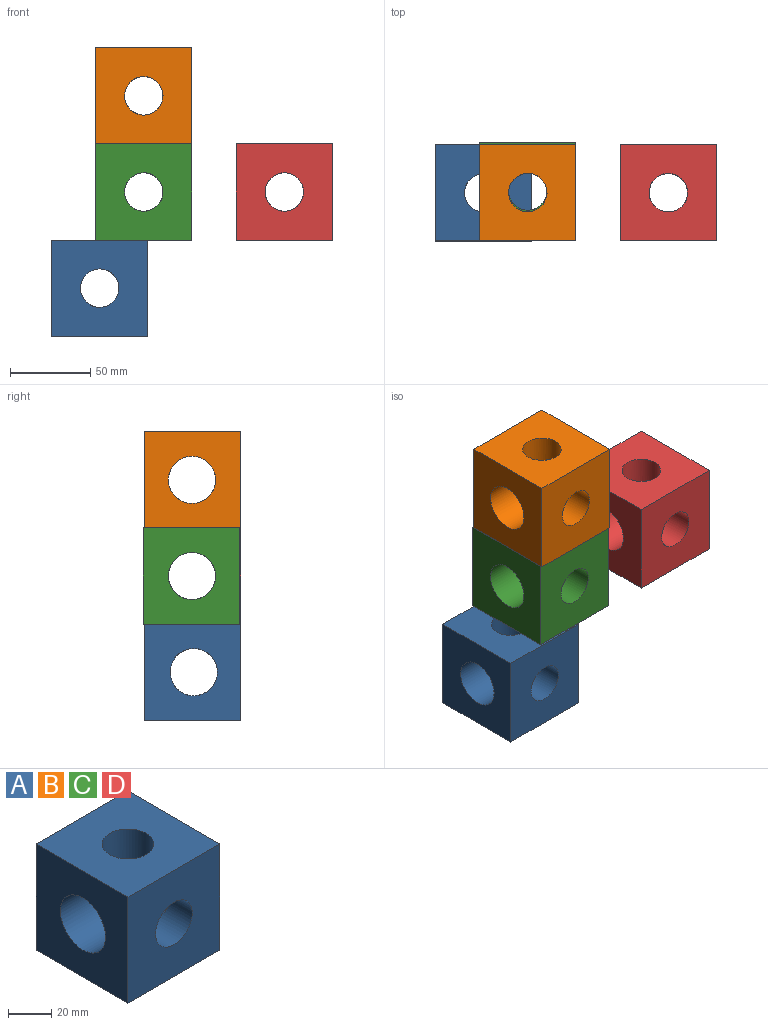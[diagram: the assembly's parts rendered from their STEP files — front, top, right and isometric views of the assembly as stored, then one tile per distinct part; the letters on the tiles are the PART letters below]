
ASSEMBLY  parts=4 mates=6
PART A: 12 faces, bbox 60x60x60 mm
  f0: cylinder r=14.74mm len=29.49mm, axis (1,0,0), area 1846.9mm2, adj f1,f4,f8,f10,f11
  f1: cylinder r=12mm len=24mm, axis (0,0,1), area 1312.2mm2, adj f0,f5,f9,f10,f11
  f2: plane 60x60mm, normal (1,0,0), area 2917mm2, adj f3,f5,f6,f7,f9
  f3: plane 60x60mm, normal (0,0,1), area 3147.6mm2, adj f2,f4,f6,f7,f8
  f4: plane 60x60mm, normal (-1,0,0), area 2917mm2, adj f0,f3,f5,f6,f7
  f5: plane 60x60mm, normal (0,0,-1), area 3147.6mm2, adj f1,f2,f4,f6,f7
  f6: plane 60x60mm, normal (0,-1,0), area 3147.6mm2, adj f2,f3,f4,f5,f11
  f7: plane 60x60mm, normal (0,1,0), area 3147.6mm2, adj f2,f3,f4,f5,f10
  f8: cylinder r=12mm len=24mm, axis (0,0,1), area 1312.2mm2, adj f0,f3,f9,f10,f11
  f9: cylinder r=14.74mm len=29.49mm, axis (1,0,0), area 1846.9mm2, adj f1,f2,f8,f10,f11
  f10: cylinder r=12mm len=24mm, axis (0,1,0), area 1339.2mm2, adj f0,f1,f7,f8,f9
  f11: cylinder r=12mm len=24mm, axis (0,1,0), area 1283.6mm2, adj f0,f1,f6,f8,f9
PART B: same geometry as A
PART C: same geometry as A
PART D: same geometry as A
PLACE A t=(-29.53,-7.09,-28.71)mm fixed
PLACE B rot(axis=(-1,0,0),180deg) t=(-2.01,-67.09,91.29)mm
PLACE C t=(-2.01,-5.99,31.29)mm
PLACE D rot(axis=(-1,0,0),180deg) t=(85.71,-67.09,31.29)mm
MATE planar A.f1 <-> D.f3  axis (0,0,1) through (-29.53,-37.09,1.29)mm
MATE cylindrical C.f0 <-> D.f0  axis (1,0,0) through (-32.01,-36.54,31.29)mm
MATE planar B.f4 <-> C.f4  axis (-1,0,0) through (-32.01,-67.09,61.29)mm
MATE planar D.f5 <-> B.f3  axis (0,0,1) through (115.71,-37.09,61.29)mm
MATE planar B.f10 <-> D.f10  axis (0,1,0) through (-2.01,-7.09,91.29)mm
MATE planar D.f10 <-> A.f10  axis (0,-1,0) through (85.71,-67.09,31.29)mm
